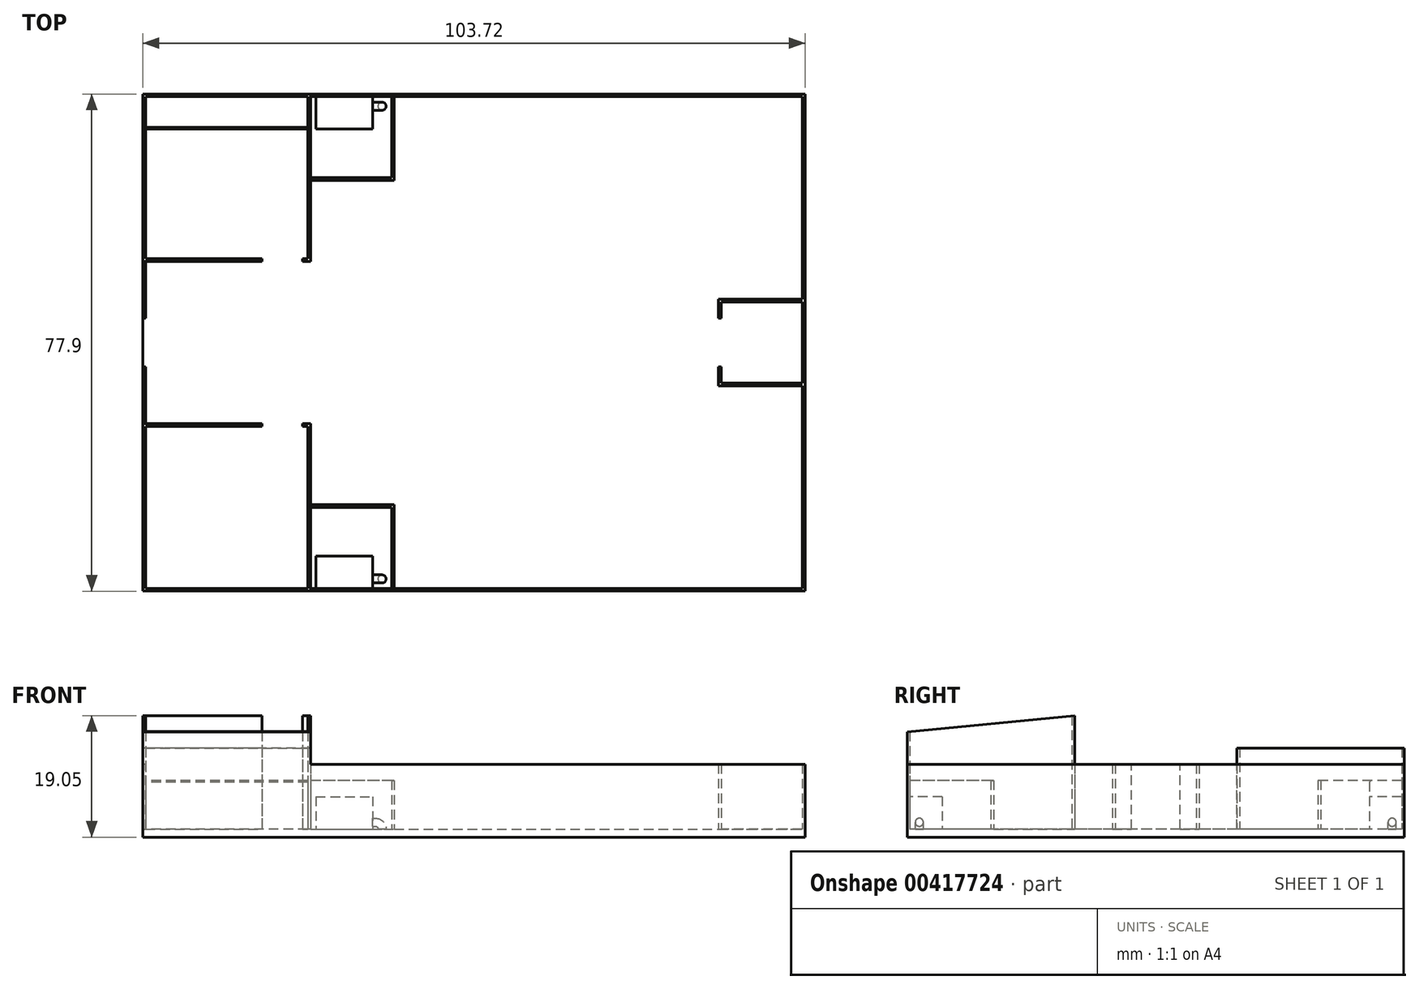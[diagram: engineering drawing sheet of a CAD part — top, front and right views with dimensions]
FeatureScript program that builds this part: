
annotation { "Feature Type Name" : "Feature", "Feature Type Description" : "" }
export const myFeature = defineFeature(function(context is Context, id is Id, definition is map)
    precondition{}
    {
        {
            var Q0;
            Q0=qCreatedBy(makeId("Top.planeOp"),FACE);
            var sketch = newSketch(context, id + "F0", { "sketchPlane" : qUnion([Q0])});
            skLineSegment(sketch, "E0.bottom", {"start": v(51.86, 38.95) * mm, "end": v(-51.86, 38.95) * mm});
            skLineSegment(sketch, "E0.top", {"start": v(51.86, -38.95) * mm, "end": v(-51.86, -38.95) * mm});
            skLineSegment(sketch, "E0.left", {"start": v(51.86, 38.95) * mm, "end": v(51.86, -38.95) * mm});
            skLineSegment(sketch, "E0.right", {"start": v(-51.86, 38.95) * mm, "end": v(-51.86, -38.95) * mm});
            skPoint(sketch, "E0.middle", {"position": v(0, 0) * mm});
            skSolve(sketch);
        }
        {
            var Q0;
            Q0 = qSketchRegion(id + "F0", true);
            extrude(context, id + "F1", {"entities" : qUnion([Q0]), "depth" : 1.27 * mm});
        }
        {
            var Q0;
            Q0=makeQuery(id+"F1.opExtrude","CAP_FACE",FACE,{"disambiguationData":[OSD([sQuery(id+"F0.wireOp",EDGE,"E0.bottom"),sQuery(id+"F0.wireOp",EDGE,"E0.top"),sQuery(id+"F0.wireOp",EDGE,"E0.left"),sQuery(id+"F0.wireOp",EDGE,"E0.right")])],"isStart":false});
            var sketch = newSketch(context, id + "F2", { "sketchPlane" : qUnion([Q0])});
            skLineSegment(sketch, "E1.bottom", {"start": v(-51.44, 38.52) * mm, "end": v(-26.04, 38.52) * mm});
            skLineSegment(sketch, "E1.top", {"start": v(-51.43, 13.12) * mm, "end": v(-26.04, 13.12) * mm});
            skLineSegment(sketch, "E1.left", {"start": v(-51.44, 38.52) * mm, "end": v(-51.44, 13.12) * mm});
            skLineSegment(sketch, "E1.right", {"start": v(-26.04, 38.52) * mm, "end": v(-26.04, 13.12) * mm});
            skLineSegment(sketch, "E2", {"start": v(-51.43, 13.12) * mm, "end": v(-51.43, -30.5) * mm});
            skLineSegment(sketch, "E3", {"start": v(-51.43, -30.5) * mm, "end": v(-51.43, -38.95) * mm});
            skLineSegment(sketch, "E4", {"start": v(-26.04, 38.52) * mm, "end": v(38.63, 38.52) * mm});
            skLineSegment(sketch, "E5", {"start": v(38.63, 38.52) * mm, "end": v(51.86, 38.52) * mm});
            skLineSegment(sketch, "E6", {"start": v(51.44, 38.52) * mm, "end": v(51.44, -38.95) * mm});
            skLineSegment(sketch, "E7", {"start": v(-51.86, -38.52) * mm, "end": v(51.43, -38.52) * mm});
            skLineSegment(sketch, "E8", {"start": v(-25.61, 38.52) * mm, "end": v(-25.61, 12.7) * mm});
            skLineSegment(sketch, "E9", {"start": v(-25.61, 12.7) * mm, "end": v(-51.43, 12.7) * mm});
            skSolve(sketch);
        }
        {
            var Q0;
            {var subQ1=sQuery(id+"F2.wireOp",EDGE,"E1.top");Q0=makeQuery(id+"F2.imprint","IMPRINT",FACE,{"disambiguationData":[TD([[makeQuery(id+"F2.imprint","IMPRINT",EDGE,{"derivedFrom":subQ1}),-1.0]])]});}
            var Q1;
            {var subQ10=sQuery(id+"F2.wireOp",EDGE,"E1.bottom");Q1=makeQuery(id+"F2.imprint","IMPRINT",FACE,{"disambiguationData":[TD([[makeQuery(id+"F2.imprint","IMPRINT",EDGE,{"derivedFrom":subQ10}),1.0]])]});}
            var Q2;
            {var subQ0=makeQuery(id+"F1.opExtrude","CAP_EDGE",EDGE,{"disambiguationData":[OSD([sQuery(id+"F0.wireOp",EDGE,"E0.left")])],"isStart":false});var subQ6=sQuery(id+"F2.wireOp",EDGE,"E5");var subQ8=makeQuery(id+"F2.imprint","INTERSECT",VERTEX,{"derivedFrom":[subQ0,subQ6]});Q2=makeQuery(id+"F2.imprint","IMPRINT",FACE,{"disambiguationData":[TD([[makeQuery(id+"F2.imprint","IMPRINT",EDGE,{"disambiguationData":[TD([[subQ8,1.0]])],"derivedFrom":subQ6}),-1.0]])]});}
            var Q3;
            {var subQ0=sQuery(id+"F2.wireOp",EDGE,"E3");var subQ1=makeQuery(id+"F1.opExtrude","CAP_EDGE",EDGE,{"disambiguationData":[OSD([sQuery(id+"F0.wireOp",EDGE,"E0.top")])],"isStart":false});var subQ2=makeQuery(id+"F2.imprint","INTERSECT",VERTEX,{"derivedFrom":[subQ1,subQ0]});Q3=makeQuery(id+"F2.imprint","IMPRINT",FACE,{"disambiguationData":[TD([[makeQuery(id+"F2.imprint","IMPRINT",EDGE,{"disambiguationData":[TD([[subQ2,1.0]])],"derivedFrom":subQ0}),1.0]])]});}
            var Q4;
            {var subQ0=sQuery(id+"F2.wireOp",EDGE,"E3");var subQ1=makeQuery(id+"F1.opExtrude","CAP_EDGE",EDGE,{"disambiguationData":[OSD([sQuery(id+"F0.wireOp",EDGE,"E0.top")])],"isStart":false});var subQ2=makeQuery(id+"F2.imprint","INTERSECT",VERTEX,{"derivedFrom":[subQ1,subQ0]});Q4=makeQuery(id+"F2.imprint","IMPRINT",FACE,{"disambiguationData":[TD([[makeQuery(id+"F2.imprint","IMPRINT",EDGE,{"disambiguationData":[TD([[subQ2,1.0]])],"derivedFrom":subQ0}),-1.0]])]});}
            extrude(context, id + "F3", {"entities" : qUnion([Q0, Q1, Q2, Q3, Q4]), "operationType" : NewBodyOperationType.ADD, "depth" : 10.16 * mm});
        }
        {
            var Q0;
            Q0=makeQuery(id+"F3.opExtrude","CAP_FACE",FACE,{"disambiguationData":[OSD([sQuery(id+"F0.wireOp",EDGE,"E0.bottom"),sQuery(id+"F0.wireOp",EDGE,"E0.top"),sQuery(id+"F0.wireOp",EDGE,"E0.left"),sQuery(id+"F0.wireOp",EDGE,"E0.right"),sQuery(id+"F2.wireOp",EDGE,"E1.bottom"),sQuery(id+"F2.wireOp",EDGE,"E1.top"),sQuery(id+"F2.wireOp",EDGE,"E1.left"),sQuery(id+"F2.wireOp",EDGE,"E1.right"),sQuery(id+"F2.wireOp",EDGE,"E2"),sQuery(id+"F2.wireOp",EDGE,"E3"),sQuery(id+"F2.wireOp",EDGE,"E4"),sQuery(id+"F2.wireOp",EDGE,"E5"),sQuery(id+"F2.wireOp",EDGE,"E6"),sQuery(id+"F2.wireOp",EDGE,"E7"),sQuery(id+"F2.wireOp",EDGE,"E8"),sQuery(id+"F2.wireOp",EDGE,"E9")])],"isStart":false});
            var sketch = newSketch(context, id + "F4", { "sketchPlane" : qUnion([Q0])});
            skLineSegment(sketch, "E10", {"start": v(-25.61, 38.52) * mm, "end": v(-25.61, 38.95) * mm});
            skLineSegment(sketch, "E11", {"start": v(-51.43, 12.7) * mm, "end": v(-51.86, 12.7) * mm});
            skSolve(sketch);
        }
        {
            var Q0;
            {var subQ1=sQuery(id+"F4.wireOp",EDGE,"E10");Q0=makeQuery(id+"F4.imprint","IMPRINT",FACE,{"disambiguationData":[TD([[makeQuery(id+"F4.imprint","IMPRINT",EDGE,{"derivedFrom":subQ1}),1.0]])]});}
            extrude(context, id + "F5", {"entities" : qUnion([Q0]), "operationType" : NewBodyOperationType.ADD, "depth" : 2.54 * mm});
        }
        {
            var Q0;
            {var subQ3=sQuery(id+"F2.wireOp",EDGE,"E8");Q0=makeQuery(id+"F2.imprint","IMPRINT",FACE,{"disambiguationData":[TD([[makeQuery(id+"F2.imprint","IMPRINT",EDGE,{"derivedFrom":subQ3}),1.0]])]});}
            var sketch = newSketch(context, id + "F6", { "sketchPlane" : qUnion([Q0])});
            skLineSegment(sketch, "E12.bottom", {"start": v(-26.04, 38.52) * mm, "end": v(-51.44, 38.52) * mm});
            skLineSegment(sketch, "E12.top", {"start": v(-26.04, 33.44) * mm, "end": v(-51.44, 33.44) * mm});
            skLineSegment(sketch, "E12.left", {"start": v(-26.04, 38.52) * mm, "end": v(-26.04, 33.44) * mm});
            skLineSegment(sketch, "E12.right", {"start": v(-51.44, 38.52) * mm, "end": v(-51.44, 33.44) * mm});
            skSolve(sketch);
        }
        {
            var Q0;
            Q0 = qSketchRegion(id + "F6", true);
            extrude(context, id + "F7", {"entities" : qUnion([Q0]), "operationType" : NewBodyOperationType.ADD, "depth" : 7.62 * mm});
        }
        {
            var Q0;
            Q0=makeQuery(id+"F7.opExtrude","CAP_EDGE",EDGE,{"disambiguationData":[OSD([sQuery(id+"F6.wireOp",EDGE,"E12.top")])],"isStart":false});
            chamfer(context, id + "F8", {"entities" : qUnion([Q0]), "width" : 0.25 * mm, "tangentPropagation" : true});
        }
        {
            var Q0;
            Q0=makeQuery(id+"F3.boolean.opBoolean","SPLIT",FACE,{"disambiguationData":[TD([makeQuery(id+"F3.opExtrude","SWEPT_FACE",FACE,{"disambiguationData":[OSD([sQuery(id+"F2.wireOp",EDGE,"E6")])]})])],"derivedFrom":makeQuery(id+"F1.opExtrude","CAP_FACE",FACE,{"disambiguationData":[OSD([sQuery(id+"F0.wireOp",EDGE,"E0.bottom"),sQuery(id+"F0.wireOp",EDGE,"E0.top"),sQuery(id+"F0.wireOp",EDGE,"E0.left"),sQuery(id+"F0.wireOp",EDGE,"E0.right")])],"isStart":false})});
            var sketch = newSketch(context, id + "F9", { "sketchPlane" : qUnion([Q0])});
            skLineSegment(sketch, "E13.bottom", {"start": v(-51.43, -38.52) * mm, "end": v(-26.03, -38.52) * mm});
            skLineSegment(sketch, "E13.top", {"start": v(-51.43, -13.12) * mm, "end": v(-26.03, -13.12) * mm});
            skLineSegment(sketch, "E13.left", {"start": v(-51.43, -38.52) * mm, "end": v(-51.43, -13.12) * mm});
            skLineSegment(sketch, "E13.right", {"start": v(-26.03, -38.52) * mm, "end": v(-26.03, -13.12) * mm});
            skLineSegment(sketch, "E14.bottom", {"start": v(-51.43, -38.52) * mm, "end": v(-25.61, -38.52) * mm});
            skLineSegment(sketch, "E14.top", {"start": v(-51.43, -12.7) * mm, "end": v(-25.61, -12.7) * mm});
            skLineSegment(sketch, "E14.left", {"start": v(-51.43, -38.52) * mm, "end": v(-51.43, -12.7) * mm});
            skLineSegment(sketch, "E14.right", {"start": v(-25.61, -38.52) * mm, "end": v(-25.61, -12.7) * mm});
            skSolve(sketch);
        }
        {
            var Q0;
            {var subQ4=sQuery(id+"F9.wireOp",EDGE,"E13.top");Q0=makeQuery(id+"F9.imprint","IMPRINT",FACE,{"disambiguationData":[TD([[makeQuery(id+"F9.imprint","IMPRINT",EDGE,{"derivedFrom":subQ4}),1.0]])]});}
            extrude(context, id + "F10", {"entities" : qUnion([Q0]), "operationType" : NewBodyOperationType.ADD, "depth" : 17.78 * mm});
        }
        {
            var Q0;
            Q0=makeQuery(id+"F3.opExtrude","CAP_FACE",FACE,{"disambiguationData":[OSD([sQuery(id+"F0.wireOp",EDGE,"E0.bottom"),sQuery(id+"F0.wireOp",EDGE,"E0.top"),sQuery(id+"F0.wireOp",EDGE,"E0.left"),sQuery(id+"F0.wireOp",EDGE,"E0.right"),sQuery(id+"F2.wireOp",EDGE,"E1.bottom"),sQuery(id+"F2.wireOp",EDGE,"E1.top"),sQuery(id+"F2.wireOp",EDGE,"E1.left"),sQuery(id+"F2.wireOp",EDGE,"E1.right"),sQuery(id+"F2.wireOp",EDGE,"E2"),sQuery(id+"F2.wireOp",EDGE,"E3"),sQuery(id+"F2.wireOp",EDGE,"E4"),sQuery(id+"F2.wireOp",EDGE,"E5"),sQuery(id+"F2.wireOp",EDGE,"E6"),sQuery(id+"F2.wireOp",EDGE,"E7"),sQuery(id+"F2.wireOp",EDGE,"E8"),sQuery(id+"F2.wireOp",EDGE,"E9")])],"isStart":false});
            var sketch = newSketch(context, id + "F11", { "sketchPlane" : qUnion([Q0])});
            skLineSegment(sketch, "E15", {"start": v(-25.61, -38.52) * mm, "end": v(-25.61, -38.95) * mm});
            skLineSegment(sketch, "E16", {"start": v(-51.43, -12.7) * mm, "end": v(-51.86, -12.7) * mm});
            skSolve(sketch);
        }
        {
            var Q0;
            Q0 = qSketchRegion(id + "F11", true);
            var Q1;
            {var subQ13=sQuery(id+"F11.wireOp",EDGE,"E15");Q1=makeQuery(id+"F11.imprint","IMPRINT",FACE,{"disambiguationData":[TD([[makeQuery(id+"F11.imprint","IMPRINT",EDGE,{"derivedFrom":subQ13}),-1.0]])]});}
            extrude(context, id + "F12", {"entities" : qUnion([Q0, Q1]), "operationType" : NewBodyOperationType.ADD, "depth" : 7.62 * mm});
        }
        {
            var Q0;
            {var subQ3=sQuery(id+"F2.wireOp",EDGE,"E8");Q0=makeQuery(id+"F2.imprint","IMPRINT",FACE,{"disambiguationData":[TD([[makeQuery(id+"F2.imprint","IMPRINT",EDGE,{"derivedFrom":subQ3}),1.0]])]});}
            var sketch = newSketch(context, id + "F13", { "sketchPlane" : qUnion([Q0])});
            skLineSegment(sketch, "E17.bottom", {"start": v(51.44, 6.35) * mm, "end": v(38.74, 6.35) * mm});
            skLineSegment(sketch, "E17.top", {"start": v(51.44, -6.35) * mm, "end": v(38.74, -6.35) * mm});
            skLineSegment(sketch, "E17.left", {"start": v(51.44, 6.35) * mm, "end": v(51.44, -6.35) * mm});
            skLineSegment(sketch, "E17.right", {"start": v(38.74, 6.35) * mm, "end": v(38.74, -6.35) * mm});
            skLineSegment(sketch, "E18.bottom", {"start": v(38.31, -6.77) * mm, "end": v(51.86, -6.77) * mm});
            skLineSegment(sketch, "E18.top", {"start": v(38.31, 6.77) * mm, "end": v(51.86, 6.77) * mm});
            skLineSegment(sketch, "E18.left", {"start": v(38.31, -6.77) * mm, "end": v(38.31, 6.77) * mm});
            skLineSegment(sketch, "E18.right", {"start": v(51.86, -6.77) * mm, "end": v(51.86, 6.77) * mm});
            skPoint(sketch, "E18.middle", {"position": v(45.09, 0) * mm});
            skLineSegment(sketch, "E19", {"start": v(38.31, 3.81) * mm, "end": v(38.74, 3.81) * mm});
            skLineSegment(sketch, "E20", {"start": v(38.31, -3.8) * mm, "end": v(38.74, -3.8) * mm});
            skSolve(sketch);
        }
        {
            var Q0;
            {var subQ5=sQuery(id+"F13.wireOp",EDGE,"E17.top");Q0=makeQuery(id+"F13.imprint","IMPRINT",FACE,{"disambiguationData":[TD([[makeQuery(id+"F13.imprint","IMPRINT",EDGE,{"derivedFrom":subQ5}),1.0]])]});}
            var Q1;
            {var subQ8=sQuery(id+"F13.wireOp",EDGE,"E17.bottom");Q1=makeQuery(id+"F13.imprint","IMPRINT",FACE,{"disambiguationData":[TD([[makeQuery(id+"F13.imprint","IMPRINT",EDGE,{"derivedFrom":subQ8}),-1.0]])]});}
            extrude(context, id + "F14", {"entities" : qUnion([Q0, Q1]), "operationType" : NewBodyOperationType.ADD, "depth" : 10.16 * mm});
        }
        {
            var Q0;
            Q0=makeQuery(id+"F12.opExtrude","CAP_EDGE",EDGE,{"disambiguationData":[OSD([sQuery(id+"F0.wireOp",EDGE,"E0.top")])],"isStart":false});
            chamfer(context, id + "F15", {"entities" : qUnion([Q0]), "chamferType" : ChamferType.TWO_OFFSETS, "width1" : 2.54 * mm, "oppositeDirection" : false, "width2" : 26.25 * mm, "tangentPropagation" : true});
        }
        {
            var Q0;
            {var subQ1=makeQuery(id+"F3.opExtrude","SWEPT_FACE",FACE,{"disambiguationData":[OSD([sQuery(id+"F2.wireOp",EDGE,"E6")])]});Q0=makeQuery(id+"F10.boolean.opBoolean","SPLIT",FACE,{"disambiguationData":[TD([subQ1])],"derivedFrom":makeQuery(id+"F3.boolean.opBoolean","SPLIT",FACE,{"disambiguationData":[TD([subQ1])],"derivedFrom":makeQuery(id+"F1.opExtrude","CAP_FACE",FACE,{"disambiguationData":[OSD([sQuery(id+"F0.wireOp",EDGE,"E0.bottom"),sQuery(id+"F0.wireOp",EDGE,"E0.top"),sQuery(id+"F0.wireOp",EDGE,"E0.left"),sQuery(id+"F0.wireOp",EDGE,"E0.right")])],"isStart":false})})});}
            var sketch = newSketch(context, id + "F16", { "sketchPlane" : qUnion([Q0])});
            skLineSegment(sketch, "E21.bottom", {"start": v(-56.78, 3.8) * mm, "end": v(-45.73, 3.8) * mm});
            skLineSegment(sketch, "E21.top", {"start": v(-56.78, -3.81) * mm, "end": v(-45.73, -3.81) * mm});
            skLineSegment(sketch, "E21.left", {"start": v(-56.78, 3.8) * mm, "end": v(-56.78, -3.81) * mm});
            skLineSegment(sketch, "E21.right", {"start": v(-45.73, 3.8) * mm, "end": v(-45.73, -3.81) * mm});
            skLineSegment(sketch, "E22.bottom", {"start": v(-33.23, 15.1) * mm, "end": v(-26.88, 15.1) * mm});
            skLineSegment(sketch, "E22.top", {"start": v(-33.23, 7.21) * mm, "end": v(-26.88, 7.21) * mm});
            skLineSegment(sketch, "E22.left", {"start": v(-33.23, 15.1) * mm, "end": v(-33.23, 7.21) * mm});
            skLineSegment(sketch, "E22.right", {"start": v(-26.88, 15.1) * mm, "end": v(-26.88, 7.21) * mm});
            skLineSegment(sketch, "E23.bottom", {"start": v(-33.23, -8.68) * mm, "end": v(-26.88, -8.68) * mm});
            skLineSegment(sketch, "E23.top", {"start": v(-33.23, -16.33) * mm, "end": v(-26.88, -16.33) * mm});
            skLineSegment(sketch, "E23.left", {"start": v(-33.23, -8.68) * mm, "end": v(-33.23, -16.33) * mm});
            skLineSegment(sketch, "E23.right", {"start": v(-26.88, -8.68) * mm, "end": v(-26.88, -16.33) * mm});
            skSolve(sketch);
        }
        {
            var Q0;
            Q0 = qSketchRegion(id + "F16", true);
            extrude(context, id + "F17", {"entities" : qUnion([Q0]), "operationType" : NewBodyOperationType.REMOVE, "depth" : 25.4 * mm});
        }
        {
            var Q0;
            {var subQ1=makeQuery(id+"F3.opExtrude","SWEPT_FACE",FACE,{"disambiguationData":[OSD([sQuery(id+"F2.wireOp",EDGE,"E6")])]});var subQ8=makeQuery(id+"F1.opExtrude","CAP_FACE",FACE,{"disambiguationData":[OSD([sQuery(id+"F0.wireOp",EDGE,"E0.bottom"),sQuery(id+"F0.wireOp",EDGE,"E0.top"),sQuery(id+"F0.wireOp",EDGE,"E0.left"),sQuery(id+"F0.wireOp",EDGE,"E0.right")])],"isStart":false});var subQ9=makeQuery(id+"F3.boolean.opBoolean","SPLIT",FACE,{"disambiguationData":[TD([subQ1])],"derivedFrom":subQ8});Q0=makeQuery(id+"F17.boolean.opBoolean","MERGE",FACE,{"derivedFrom":[makeQuery(id+"F3.boolean.opBoolean","SPLIT",FACE,{"disambiguationData":[TD([makeQuery(id+"F3.opExtrude","SWEPT_FACE",FACE,{"disambiguationData":[OSD([sQuery(id+"F2.wireOp",EDGE,"E1.bottom")])]})])],"derivedFrom":subQ8}),makeQuery(id+"F10.boolean.opBoolean","SPLIT",FACE,{"disambiguationData":[TD([makeQuery(id+"F10.opExtrude","SWEPT_FACE",FACE,{"disambiguationData":[OSD([sQuery(id+"F9.wireOp",EDGE,"E13.top")])]})])],"derivedFrom":subQ9}),makeQuery(id+"F10.boolean.opBoolean","SPLIT",FACE,{"disambiguationData":[TD([subQ1])],"derivedFrom":subQ9}),makeQuery(id+"F17.opExtrude","CAP_FACE",FACE,{"disambiguationData":[OSD([sQuery(id+"F16.wireOp",EDGE,"E21.bottom"),sQuery(id+"F16.wireOp",EDGE,"E21.top"),sQuery(id+"F16.wireOp",EDGE,"E21.left"),sQuery(id+"F16.wireOp",EDGE,"E21.right")])],"isStart":true}),makeQuery(id+"F17.opExtrude","CAP_FACE",FACE,{"disambiguationData":[OSD([sQuery(id+"F16.wireOp",EDGE,"E22.bottom"),sQuery(id+"F16.wireOp",EDGE,"E22.top"),sQuery(id+"F16.wireOp",EDGE,"E22.left"),sQuery(id+"F16.wireOp",EDGE,"E22.right")])],"isStart":true}),makeQuery(id+"F17.opExtrude","CAP_FACE",FACE,{"disambiguationData":[OSD([sQuery(id+"F16.wireOp",EDGE,"E23.bottom"),sQuery(id+"F16.wireOp",EDGE,"E23.top"),sQuery(id+"F16.wireOp",EDGE,"E23.left"),sQuery(id+"F16.wireOp",EDGE,"E23.right")])],"isStart":true})]});}
            var sketch = newSketch(context, id + "F18", { "sketchPlane" : qUnion([Q0])});
            skCircle(sketch, "E24", {"center": v(-14.4, 37.04) * mm, "radius": 0.64 * mm});
            skCircle(sketch, "E25", {"center": v(-14.4, -37.04) * mm, "radius": 0.64 * mm});
            skLineSegment(sketch, "E26", {"start": v(-12.91, 38.52) * mm, "end": v(-12.91, 25.82) * mm});
            skLineSegment(sketch, "E27", {"start": v(-12.49, 38.52) * mm, "end": v(-12.49, 25.4) * mm});
            skLineSegment(sketch, "E28", {"start": v(-12.91, 25.82) * mm, "end": v(-25.61, 25.82) * mm});
            skLineSegment(sketch, "E29", {"start": v(-12.49, 25.4) * mm, "end": v(-25.61, 25.4) * mm});
            skPoint(sketch, "E30", {"position": v(-15.03, 37.04) * mm});
            skLineSegment(sketch, "E31", {"start": v(-15.45, 37.04) * mm, "end": v(-15.45, 38.14) * mm});
            skLineSegment(sketch, "E32", {"start": v(-25.61, -25.82) * mm, "end": v(-12.91, -25.82) * mm});
            skLineSegment(sketch, "E33", {"start": v(-12.91, -25.82) * mm, "end": v(-12.91, -38.52) * mm});
            skLineSegment(sketch, "E34", {"start": v(-25.61, -25.4) * mm, "end": v(-12.49, -25.4) * mm});
            skLineSegment(sketch, "E35", {"start": v(-12.49, -25.4) * mm, "end": v(-12.49, -38.52) * mm});
            skLineSegment(sketch, "E36", {"start": v(-15.45, -35.72) * mm, "end": v(-15.45, -37.04) * mm});
            skSolve(sketch);
        }
        {
            var Q0;
            {var subQ4=sQuery(id+"F18.wireOp",EDGE,"E26");Q0=makeQuery(id+"F18.imprint","IMPRINT",FACE,{"disambiguationData":[TD([[makeQuery(id+"F18.imprint","IMPRINT",EDGE,{"derivedFrom":subQ4}),1.0]])]});}
            var Q1;
            {var subQ3=sQuery(id+"F18.wireOp",EDGE,"E32");Q1=makeQuery(id+"F18.imprint","IMPRINT",FACE,{"disambiguationData":[TD([[makeQuery(id+"F18.imprint","IMPRINT",EDGE,{"derivedFrom":subQ3}),1.0]])]});}
            extrude(context, id + "F19", {"entities" : qUnion([Q0, Q1]), "operationType" : NewBodyOperationType.ADD, "depth" : 7.62 * mm});
        }
        {
            var Q0;
            Q0=makeQuery(id+"F18.imprint","IMPRINT",FACE,{"disambiguationData":[TD([[makeQuery(id+"F18.imprint","IMPRINT",EDGE,{"derivedFrom":sQuery(id+"F18.wireOp",EDGE,"E24")}),1.0]])]});
            var Q1;
            Q1=makeQuery(id+"F18.imprint","IMPRINT",FACE,{"disambiguationData":[TD([[makeQuery(id+"F18.imprint","IMPRINT",EDGE,{"derivedFrom":sQuery(id+"F18.wireOp",EDGE,"E25")}),1.0]])]});
            var Q2;
            Q2=sQuery(id+"F18.wireOp",EDGE,"E31");
            revolve(context, id + "F20", {"operationType" : NewBodyOperationType.ADD, "entities" : qUnion([Q0, Q1]), "axis" : qUnion([Q2]), "revolveType" : RevolveType.ONE_DIRECTION, "oppositeDirection" : true, "angle" : 90 * degree});
        }
        {
            var Q0;
            Q0=makeQuery(id+"F18.imprint","IMPRINT",FACE,{"disambiguationData":[TD([[makeQuery(id+"F18.imprint","IMPRINT",EDGE,{"derivedFrom":sQuery(id+"F18.wireOp",EDGE,"E25")}),-1.0]])]});
            var sketch = newSketch(context, id + "F21", { "sketchPlane" : qUnion([Q0])});
            skLineSegment(sketch, "E37.bottom", {"start": v(-24.77, 38.52) * mm, "end": v(-15.88, 38.52) * mm});
            skLineSegment(sketch, "E37.top", {"start": v(-24.77, 33.44) * mm, "end": v(-15.88, 33.44) * mm});
            skLineSegment(sketch, "E37.left", {"start": v(-24.77, 38.52) * mm, "end": v(-24.77, 33.44) * mm});
            skLineSegment(sketch, "E37.right", {"start": v(-15.88, 38.52) * mm, "end": v(-15.88, 33.44) * mm});
            skLineSegment(sketch, "E38.bottom", {"start": v(-24.76, -33.44) * mm, "end": v(-15.87, -33.44) * mm});
            skLineSegment(sketch, "E38.top", {"start": v(-24.76, -38.52) * mm, "end": v(-15.87, -38.52) * mm});
            skLineSegment(sketch, "E38.left", {"start": v(-24.76, -33.44) * mm, "end": v(-24.76, -38.52) * mm});
            skLineSegment(sketch, "E38.right", {"start": v(-15.87, -33.44) * mm, "end": v(-15.87, -38.52) * mm});
            skSolve(sketch);
        }
        {
            var Q0;
            Q0=makeQuery(id+"F21.imprint","IMPRINT",FACE,{"disambiguationData":[TD([[makeQuery(id+"F21.imprint","IMPRINT",EDGE,{"derivedFrom":sQuery(id+"F21.wireOp",EDGE,"E37.bottom")}),-1.0]])]});
            var Q1;
            Q1=makeQuery(id+"F21.imprint","IMPRINT",FACE,{"disambiguationData":[TD([[makeQuery(id+"F21.imprint","IMPRINT",EDGE,{"derivedFrom":sQuery(id+"F21.wireOp",EDGE,"E38.bottom")}),-1.0]])]});
            extrude(context, id + "F22", {"entities" : qUnion([Q0, Q1]), "operationType" : NewBodyOperationType.ADD, "depth" : 5.08 * mm});
        }
        {
            var Q0;
            Q0=makeQuery(id+"F20.opRevolve","CAP_FACE",FACE,{"disambiguationData":[OSD([sQuery(id+"F18.wireOp",EDGE,"E24")])],"isStart":false});
            var Q1;
            Q1=makeQuery(id+"F20.opRevolve","CAP_FACE",FACE,{"disambiguationData":[OSD([sQuery(id+"F18.wireOp",EDGE,"E25")])],"isStart":false});
            extrude(context, id + "F23", {"entities" : qUnion([Q0, Q1]), "operationType" : NewBodyOperationType.ADD, "depth" : 2.54 * mm});
        }
    });
